FCSTD DOCUMENT  (FreeCAD 1.0RUnknown)
Label: rightWallSide
License: All rights reserved
LicenseURL: https://en.wikipedia.org/wiki/All_rights_reserved
objects: App::Link×4, App::DocumentObjectGroup×3, PartDesign::CoordinateSystem×1, App::FeaturePython×1, App::Part×1
note: 1 computed .brp shape members not serialized (recipe doc carries the construction recipe); baked Part::Feature solids carry a one-line shape summary decoded from their .brp
EXTERNAL_REF file=beam60x100x919.FCStd obj=LCS_Origin
EXTERNAL_REF file=beam60x100x919.FCStd obj=beam60x100x887
EXTERNAL_REF file=beam60x100x1000.FCStd obj=LCS_1
EXTERNAL_REF file=beam60x100x919.FCStd obj=LCS_1
EXTERNAL_REF file=beam60x100x1000.FCStd obj=beam60x100x887
EXTERNAL_REF file=beam60x100x1000.FCStd obj=LCS_2
EXTERNAL_REF file=beam60x100x919.FCStd obj=LCS_2

FEATURE [App::DocumentObjectGroup] Parts
FEATURE [PartDesign::CoordinateSystem] LCS_Origin
  AttacherType = Attacher::AttachEngine3D
  AttachmentSupport = -> [X_Axis]
  MapMode = 2
FEATURE [App::DocumentObjectGroup] Constraints
FEATURE [App::FeaturePython] Variables  # WARN: FeaturePython — macro-defined, semantics opaque (R4)
  Type = App::PropertyContainer
FEATURE [App::DocumentObjectGroup] Configurations
FEATURE [App::Link] beam60x100x1100
  AttachedBy = #LCS_Origin
  AttachedTo = Parent Assembly#LCS_Origin
  AttachmentOffset = pos=(0,0,0) rot=(0,1,0;1.5708rad)
  LinkPlacement = pos=(0,0,0) rot=(0,1,0;1.5708rad)
  LinkedObject = -> <external beam60x100x919.FCStd>#beam60x100x887
  Placement = pos=(0,0,0) rot=(0,1,0;1.5708rad)
  SolverId = Asm4EE
  expr: Placement = LCS_Origin.Placement * AttachmentOffset * beam60x100x919#LCS_Origin.Placement ^ -1
FEATURE [App::Link] beam60x100x800
  AttachedBy = #LCS_1
  AttachedTo = beam60x100x1100#LCS_1
  AttachmentOffset = pos=(0,0,0) rot=(0,0,1;4.71239rad)
  LinkPlacement = pos=(-1.087e-13,429.5,470) rot=(0.57735,-0.57735,0.57735;4.18879rad)
  LinkedObject = -> <external beam60x100x1000.FCStd>#beam60x100x887
  Placement = pos=(-1.087e-13,429.5,470) rot=(0.57735,-0.57735,0.57735;4.18879rad)
  SolverId = Asm4EE
  expr: Placement = beam60x100x1100.Placement * beam60x100x919#LCS_1.Placement * AttachmentOffset * beam60x100x1000#LCS_1.Placement ^ -1
FEATURE [App::Link] beam60x100x1101
  AttachedBy = #LCS_2
  AttachedTo = beam60x100x1100#LCS_2
  AttachmentOffset = pos=(0,0,0) rot=(0,0,1;1.5708rad)
  LinkPlacement = pos=(-1e-13,-429.5,470) rot=(0.57735,0.57735,0.57735;2.0944rad)
  LinkedObject = -> <external beam60x100x1000.FCStd>#beam60x100x887
  Placement = pos=(-1e-13,-429.5,470) rot=(0.57735,0.57735,0.57735;2.0944rad)
  SolverId = Asm4EE
  expr: Placement = beam60x100x1100.Placement * beam60x100x919#LCS_2.Placement * AttachmentOffset * beam60x100x1000#LCS_2.Placement ^ -1
FEATURE [App::Link] beam60x100x1102
  AttachedBy = #LCS_2
  AttachedTo = beam60x100x800#LCS_2
  AttachmentOffset = pos=(0,0,0) rot=(0,0,1;4.71239rad)
  LinkPlacement = pos=(-2.174e-13,2.274e-13,940) rot=(-0.707107,0,-0.707107;3.14159rad)
  LinkedObject = -> <external beam60x100x919.FCStd>#beam60x100x887
  Placement = pos=(-2.174e-13,2.274e-13,940) rot=(-0.707107,0,-0.707107;3.14159rad)
  SolverId = Asm4EE
  expr: Placement = beam60x100x800.Placement * beam60x100x1000#LCS_2.Placement * AttachmentOffset * beam60x100x919#LCS_2.Placement ^ -1
FEATURE [App::Part] Assembly  label="rightWallSide"
  AssemblyType = Part::Link
  Group = -> [LCS_Origin,Constraints,Variables,Configurations,beam60x100x1100,beam60x100x800,beam60x100x1101,beam60x100x1102]
  Origin = -> Origin
  Type = Assembly

RESOLVED EXTERNAL PARTS (link-assembly join: the EXTERNAL_REF files above that resolve inside this repo's crawl, each included once):
---- part beam60x100x1000.FCStd = doc fcstd_e8d18024eead ----
FCSTD DOCUMENT  (FreeCAD 1.0RUnknown)
Label: beam60x100x1000
License: All rights reserved
LicenseURL: https://en.wikipedia.org/wiki/All_rights_reserved
objects: PartDesign::CoordinateSystem×3, Sketcher::SketchObject×1, PartDesign::Pad×1, PartDesign::Body×1, App::Part×1
note: 9 computed .brp shape members not serialized (recipe doc carries the construction recipe); baked Part::Feature solids carry a one-line shape summary decoded from their .brp

FEATURE [Sketcher::SketchObject] Sketch
  ArcFitTolerance = 1e-06
  AttachmentSupport = -> [XZ_Plane]
  FullyConstrained = true
  MakeInternals = false
  MapMode = 5
  Placement = pos=(0,0,0) rot=(1,0,0;1.5708rad)
  sketch-geometry (5):
    g0: LineSegment StartX=-30 StartY=-50 StartZ=0 EndX=30 EndY=-50 EndZ=0
    g1: LineSegment StartX=30 StartY=-50 StartZ=0 EndX=30 EndY=50 EndZ=0
    g2: LineSegment StartX=30 StartY=50 StartZ=0 EndX=-30 EndY=50 EndZ=0
    g3: LineSegment StartX=-30 StartY=50 StartZ=0 EndX=-30 EndY=-50 EndZ=0
    g4: GeomPoint [constr] X=0 Y=0 Z=0
  constraints (12):
    c: Coincident(g0,g1)
    c: Coincident(g1,g2)
    c: Coincident(g2,g3)
    c: Coincident(g3,g0)
    c: Horizontal(g0)
    c: Horizontal(g2)
    c: Vertical(g1)
    c: Vertical(g3)
    c: Symmetric(g2,g0,g4)
    c: Coincident(g4,g-1)
    c: DistanceX(g0,g0) = 60
    c: DistanceY(g3,g3) = 100
FEATURE [PartDesign::Pad] Pad
  Direction = (0,-1,2e-16)
  Length = 880
  Length2 = 10
  Midplane = true
  Placement = pos=(0,0,0) rot=(1,0,0;1.5708rad)
  Profile = -> Sketch
  ReferenceAxis = -> Sketch [N_Axis]
  Refine = true
  Suppressed = false
  Type = 0
FEATURE [PartDesign::Body] Body  label="Körper"
  AllowCompound = false
  Group = -> [Sketch,Pad]
  Origin = -> Origin
  Tip = -> Pad
FEATURE [PartDesign::CoordinateSystem] LCS_Origin
  AttacherType = Attacher::AttachEngine3D
  AttachmentSupport = -> [X_Axis001]
  MapMode = 2
FEATURE [PartDesign::CoordinateSystem] LCS_1
  AttacherType = Attacher::AttachEngine3D
  AttachmentSupport = -> [Pad]
  MapMode = 45
  Placement = pos=(-30,440,-1.95e-13) rot=(0,0,1;0rad)
FEATURE [PartDesign::CoordinateSystem] LCS_2
  AttacherType = Attacher::AttachEngine3D
  AttachmentSupport = -> [Pad]
  MapMode = 45
  Placement = pos=(-30,-440,1.96e-13) rot=(0,0,1;0rad)
FEATURE [App::Part] beam60x100x887  label="beam60x100x800"
  Group = -> [LCS_Origin,Body,LCS_1,LCS_2]
  Origin = -> Origin001
---- part beam60x100x919.FCStd = doc fcstd_d0cb0fe0bb71 ----
FCSTD DOCUMENT  (FreeCAD 1.0RUnknown)
Label: beam60x100x919
License: All rights reserved
LicenseURL: https://en.wikipedia.org/wiki/All_rights_reserved
objects: PartDesign::CoordinateSystem×3, Sketcher::SketchObject×1, PartDesign::Pad×1, PartDesign::Body×1, App::Part×1
note: 9 computed .brp shape members not serialized (recipe doc carries the construction recipe); baked Part::Feature solids carry a one-line shape summary decoded from their .brp

FEATURE [Sketcher::SketchObject] Sketch
  ArcFitTolerance = 1e-06
  AttachmentSupport = -> [XZ_Plane]
  FullyConstrained = true
  MakeInternals = false
  MapMode = 5
  Placement = pos=(0,0,0) rot=(1,0,0;1.5708rad)
  sketch-geometry (5):
    g0: LineSegment StartX=-30 StartY=-50 StartZ=0 EndX=30 EndY=-50 EndZ=0
    g1: LineSegment StartX=30 StartY=-50 StartZ=0 EndX=30 EndY=50 EndZ=0
    g2: LineSegment StartX=30 StartY=50 StartZ=0 EndX=-30 EndY=50 EndZ=0
    g3: LineSegment StartX=-30 StartY=50 StartZ=0 EndX=-30 EndY=-50 EndZ=0
    g4: GeomPoint [constr] X=0 Y=0 Z=0
  constraints (12):
    c: Coincident(g0,g1)
    c: Coincident(g1,g2)
    c: Coincident(g2,g3)
    c: Coincident(g3,g0)
    c: Horizontal(g0)
    c: Horizontal(g2)
    c: Vertical(g1)
    c: Vertical(g3)
    c: Symmetric(g2,g0,g4)
    c: Coincident(g4,g-1)
    c: DistanceX(g0,g0) = 60
    c: DistanceY(g3,g3) = 100
FEATURE [PartDesign::Pad] Pad
  Direction = (0,-1,2e-16)
  Length = 919
  Length2 = 10
  Midplane = true
  Placement = pos=(0,0,0) rot=(1,0,0;1.5708rad)
  Profile = -> Sketch
  ReferenceAxis = -> Sketch [N_Axis]
  Refine = true
  Suppressed = false
  Type = 0
FEATURE [PartDesign::Body] Body  label="Körper"
  AllowCompound = false
  Group = -> [Sketch,Pad]
  Origin = -> Origin
  Tip = -> Pad
FEATURE [PartDesign::CoordinateSystem] LCS_Origin
  AttacherType = Attacher::AttachEngine3D
  AttachmentSupport = -> [X_Axis001]
  MapMode = 2
FEATURE [PartDesign::CoordinateSystem] LCS_1
  AttacherType = Attacher::AttachEngine3D
  AttachmentSupport = -> [Pad]
  MapMode = 45
  Placement = pos=(-30,459.5,-2.04e-13) rot=(0,0,1;0rad)
FEATURE [PartDesign::CoordinateSystem] LCS_2
  AttacherType = Attacher::AttachEngine3D
  AttachmentSupport = -> [Pad]
  MapMode = 45
  Placement = pos=(-30,-459.5,2.04e-13) rot=(0,0,1;0rad)
FEATURE [App::Part] beam60x100x887  label="beam60x100x1100"
  Group = -> [LCS_Origin,Body,LCS_1,LCS_2]
  Origin = -> Origin001
